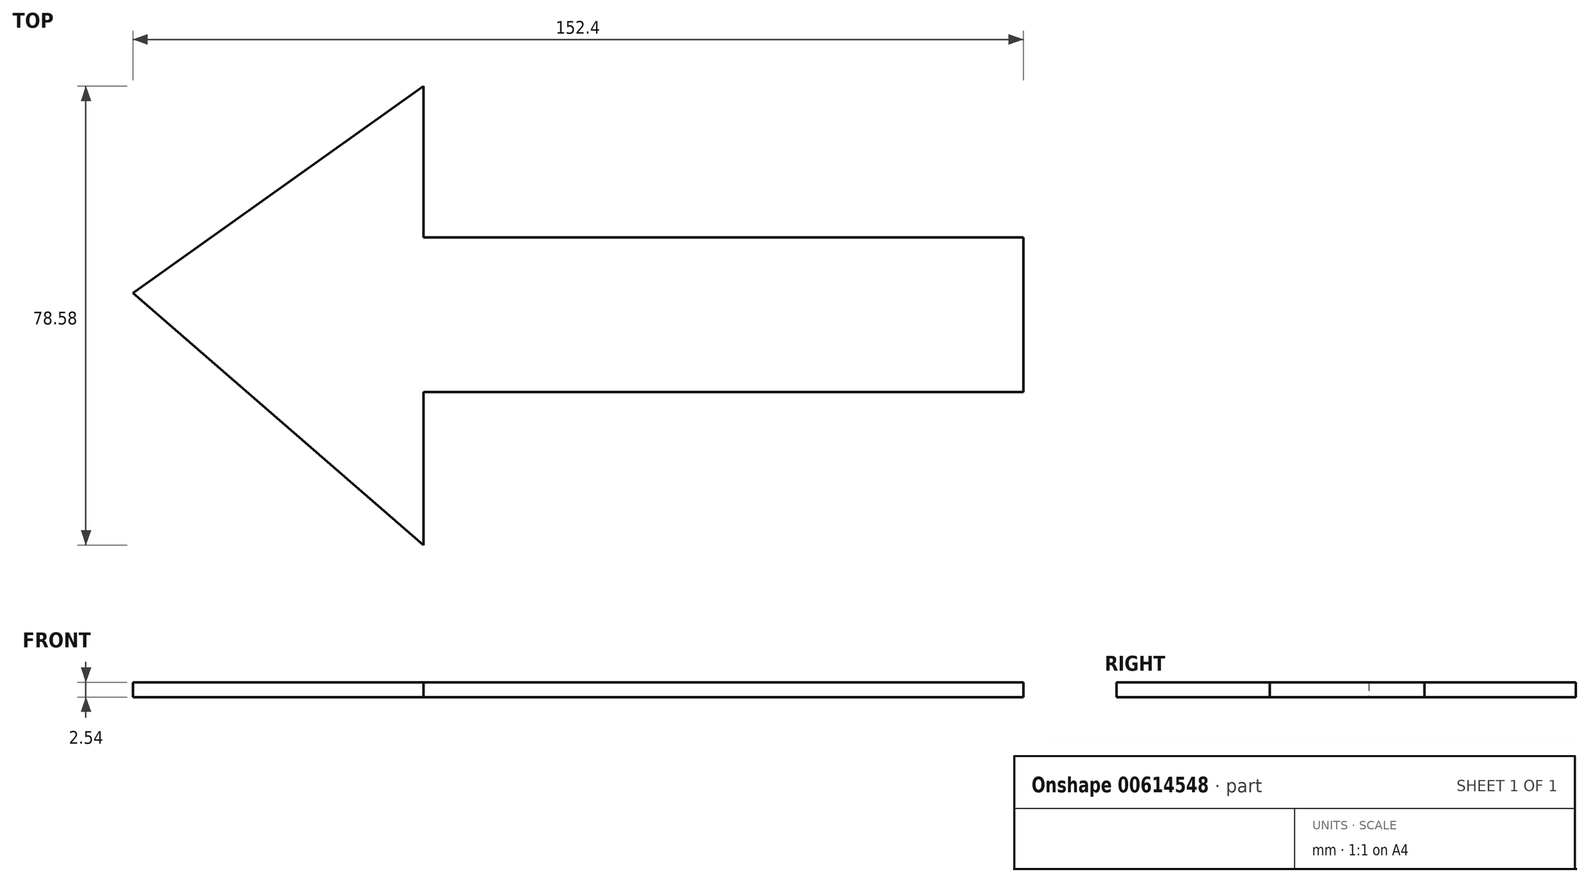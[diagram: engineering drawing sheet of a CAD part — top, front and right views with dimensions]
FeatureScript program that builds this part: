
annotation { "Feature Type Name" : "Feature", "Feature Type Description" : "" }
export const myFeature = defineFeature(function(context is Context, id is Id, definition is map)
    precondition{}
    {
        {
            var Q0;
            Q0=qCreatedBy(makeId("Top.planeOp"),FACE);
            var sketch = newSketch(context, id + "F0", { "sketchPlane" : qUnion([Q0])});
            skLineSegment(sketch, "E0.bottom", {"start": v(-50.26, 13.65) * mm, "end": v(52.4, 13.65) * mm});
            skLineSegment(sketch, "E0.top", {"start": v(-50.26, -12.8) * mm, "end": v(52.4, -12.8) * mm});
            skLineSegment(sketch, "E0.left", {"start": v(-50.26, 13.65) * mm, "end": v(-50.26, -12.8) * mm});
            skLineSegment(sketch, "E0.right", {"start": v(52.4, 13.65) * mm, "end": v(52.4, -12.8) * mm});
            skLineSegment(sketch, "E1", {"start": v(-50.26, 13.65) * mm, "end": v(-50.26, 39.58) * mm});
            skLineSegment(sketch, "E2", {"start": v(-50.26, 39.58) * mm, "end": v(-100, 4.13) * mm});
            skLineSegment(sketch, "E3", {"start": v(-100, 4.13) * mm, "end": v(-50.26, -39) * mm});
            skLineSegment(sketch, "E4", {"start": v(-50.26, -39) * mm, "end": v(-50.26, -12.8) * mm});
            skSolve(sketch);
        }
        {
            var Q0;
            Q0 = qSketchRegion(id + "F0", true);
            extrude(context, id + "F1", {"entities" : qUnion([Q0]), "depth" : 2.54 * mm, "offsetDistance" : 25.4 * mm});
        }
    });
